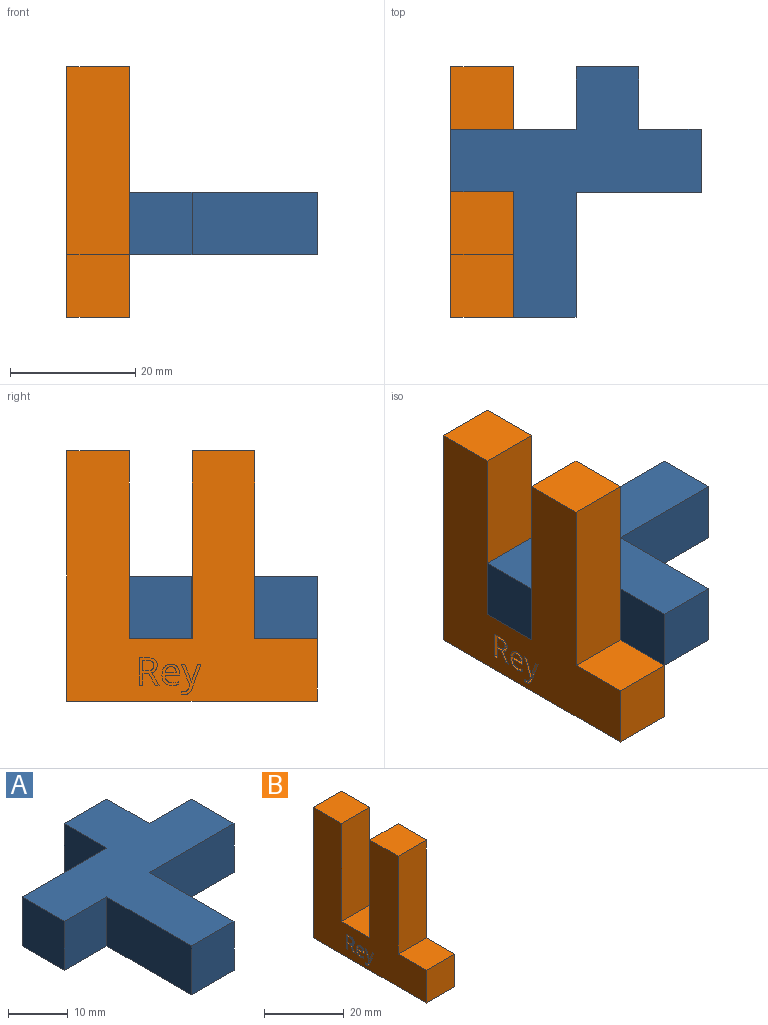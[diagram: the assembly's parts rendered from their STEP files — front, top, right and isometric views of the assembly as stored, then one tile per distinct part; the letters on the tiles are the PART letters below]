
ASSEMBLY  parts=2 mates=1
PART A: 14 faces, bbox 40x40x10 mm
  f0: plane 10x10mm, normal (1,0,0), area 100mm2, adj f3,f8,f9,f13
  f1: plane 10x10mm, normal (-1,0,0), area 100mm2, adj f3,f5,f11,f13
  f2: plane 10x10mm, normal (0,-1,0), area 100mm2, adj f3,f10,f12,f13
  f3: plane 40x40mm, normal (0,0,1), area 700mm2, adj f0,f1,f2,f4,f5,f6,f7,f8
  f4: plane 10x10mm, normal (0,1,0), area 100mm2, adj f3,f6,f7,f13
  f5: plane 20x10mm, normal (0,1,0), area 200mm2, adj f1,f3,f6,f13
  f6: plane 10x10mm, normal (-1,0,0), area 100mm2, adj f3,f4,f5,f13
  f7: plane 10x10mm, normal (1,0,0), area 100mm2, adj f3,f4,f8,f13
  f8: plane 10x10mm, normal (0,1,0), area 100mm2, adj f0,f3,f7,f13
  f9: plane 20x10mm, normal (0,-1,0), area 200mm2, adj f0,f3,f10,f13
  f10: plane 20x10mm, normal (1,0,0), area 200mm2, adj f2,f3,f9,f13
  f11: plane 10x10mm, normal (0,-1,0), area 100mm2, adj f1,f3,f12,f13
  f12: plane 20x10mm, normal (-1,0,0), area 200mm2, adj f2,f3,f11,f13
  f13: plane 40x40mm, normal (0,0,-1), area 700mm2, adj f0,f1,f2,f4,f5,f6,f7,f8
PART B: 70 faces, bbox 10x40x40 mm
  f0: plane 40x40mm, normal (-1,0,0), area 981.5mm2, adj f1,f2,f3,f4,f5,f7,f8,f9
  f1: plane 10x10mm, normal (0,0,1), area 100mm2, adj f0,f6,f7,f11
  f2: plane 10x10mm, normal (0,0,1), area 100mm2, adj f0,f4,f6,f8
  f3: plane 10x10mm, normal (0,-1,0), area 100mm2, adj f0,f5,f6,f10
  f4: plane 40x10mm, normal (0,1,0), area 400mm2, adj f0,f2,f5,f6
  f5: plane 40x10mm, normal (0,0,-1), area 400mm2, adj f0,f3,f4,f6
  f6: plane 40x40mm, normal (1,0,0), area 1000mm2, adj f1,f2,f3,f4,f5,f7,f8,f9
  f7: plane 30x10mm, normal (0,1,0), area 300mm2, adj f0,f1,f6,f9
  f8: plane 30x10mm, normal (0,-1,0), area 300mm2, adj f0,f2,f6,f9
  f9: plane 10x10mm, normal (0,0,1), area 100mm2, adj f0,f6,f7,f8
  f10: plane 10x10mm, normal (0,0,1), area 100mm2, adj f0,f3,f6,f11
  f11: plane 30x10mm, normal (0,-1,0), area 300mm2, adj f0,f1,f6,f10
  f12: extruded ~2x0.64mm, area 1.4mm2, adj f13,f30,f31,f68
  f13: extruded ~2x0.6mm, area 1.4mm2, adj f12,f14,f31,f68
  f14: extruded ~2x0.73mm, area 1.5mm2, adj f13,f15,f31,f68
  f15: plane 2x1.73mm, normal (0,0,-1), area 3.5mm2, adj f14,f30,f31,f68
  f16: extruded ~2x1.16mm, area 2.6mm2, adj f0,f17,f29,f31
  f17: extruded ~2x0.57mm, area 1.2mm2, adj f0,f16,f18,f31
  f18: extruded ~2x0.5mm, area 1.1mm2, adj f0,f17,f19,f31
  f19: plane 2x0.45mm, normal (0,1,0), area 0.9mm2, adj f0,f18,f20,f31
  f20: extruded ~2x1.06mm, area 2.2mm2, adj f0,f19,f21,f31
  f21: extruded ~2x0.79mm, area 1.7mm2, adj f0,f20,f22,f31
  f22: extruded ~2x0.89mm, area 1.9mm2, adj f0,f21,f23,f31
  f23: plane 2.28x2mm, normal (0,0,1), area 4.6mm2, adj f0,f22,f24,f31
  f24: plane 2x0.32mm, normal (0,1,0), area 0.6mm2, adj f0,f23,f25,f31
  f25: extruded ~2x1.08mm, area 2.3mm2, adj f0,f24,f26,f31
  f26: extruded ~2x0.98mm, area 2.2mm2, adj f0,f25,f27,f31
  f27: extruded ~2x1.06mm, area 2.4mm2, adj f0,f26,f28,f31
  f28: extruded ~2x1.27mm, area 2.7mm2, adj f0,f27,f29,f31
  f29: extruded ~2x1.24mm, area 2.7mm2, adj f0,f16,f28,f31
  f30: extruded ~2x0.72mm, area 1.6mm2, adj f12,f15,f31,f68
  f31: plane 3.43x2.8mm, normal (-1,0,0), area 4.4mm2, adj f12,f13,f14,f15,f16,f17,f18,f19
  f32: plane 2x0.7mm, normal (0,0,-1), area 1.4mm2, adj f33,f49,f50,f69
  f33: plane 2x1.69mm, normal (0,1,0), area 3.4mm2, adj f32,f34,f50,f69
  f34: plane 2x0.67mm, normal (0,0,1), area 1.3mm2, adj f33,f35,f50,f69
  f35: extruded ~2x0.83mm, area 1.7mm2, adj f34,f36,f50,f69
  f36: extruded ~2x0.63mm, area 1.4mm2, adj f35,f37,f50,f69
  f37: extruded ~2x0.65mm, area 1.4mm2, adj f36,f49,f50,f69
  f38: plane 2x1.84mm, normal (0,1,0), area 3.7mm2, adj f0,f39,f48,f50
  f39: plane 2x0.92mm, normal (0,0,1), area 1.8mm2, adj f0,f38,f40,f50
  f40: plane 2x1.84mm, normal (0,-0.86,0.5), area 4.2mm2, adj f0,f39,f41,f50
  f41: plane 2x0.61mm, normal (0,0,1), area 1.2mm2, adj f0,f40,f42,f50
  f42: plane 2x1.98mm, normal (0,0.86,-0.52), area 4.6mm2, adj f0,f41,f43,f50
  f43: extruded ~2x1.18mm, area 3.2mm2, adj f0,f42,f44,f50
  f44: extruded ~2x0.94mm, area 2.1mm2, adj f0,f43,f45,f50
  f45: extruded ~2x1.2mm, area 2.5mm2, adj f0,f44,f46,f50
  f46: plane 2x1.21mm, normal (0,0,-1), area 2.4mm2, adj f0,f45,f47,f50
  f47: plane 4.42x2mm, normal (0,-1,0), area 8.8mm2, adj f0,f46,f48,f50
  f48: plane 2x0.51mm, normal (0,0,1), area 1mm2, adj f0,f38,f47,f50
  f49: extruded ~2x0.8mm, area 1.7mm2, adj f32,f37,f50,f69
  f50: plane 4.42x3.11mm, normal (-1,0,0), area 5.8mm2, adj f32,f33,f34,f35,f36,f37,f38,f39
  f51: plane 2x0.54mm, normal (0,0,-1), area 1.1mm2, adj f0,f52,f66,f67
  f52: plane 3.33x2mm, normal (0,-0.93,0.37), area 7.2mm2, adj f0,f51,f53,f67
  f53: plane 2x0.47mm, normal (0,-0.93,-0.37), area 1mm2, adj f0,f52,f54,f67
  f54: extruded ~2x0.74mm, area 2mm2, adj f0,f53,f55,f67
  f55: extruded ~2x0.37mm, area 0.7mm2, adj f0,f54,f56,f67
  f56: plane 2x0.4mm, normal (0,-1,0), area 0.8mm2, adj f0,f55,f57,f67
  f57: extruded ~2x0.45mm, area 0.9mm2, adj f0,f56,f58,f67
  f58: extruded ~2x0.69mm, area 1.5mm2, adj f0,f57,f59,f67
  f59: extruded ~2x0.79mm, area 1.9mm2, adj f0,f58,f60,f67
  f60: plane 3.77x2mm, normal (0,0.94,0.35), area 8.1mm2, adj f0,f59,f61,f67
  f61: plane 2x0.54mm, normal (0,0,-1), area 1.1mm2, adj f0,f60,f62,f67
  f62: extruded ~2.29x2mm, area 4.9mm2, adj f0,f61,f63,f67
  f63: extruded ~2x0.53mm, area 1.1mm2, adj f0,f62,f64,f67
  f64: plane 2x0.02mm, normal (0,0,-1), area 0mm2, adj f0,f63,f65,f67
  f65: extruded ~2x0.93mm, area 2mm2, adj f0,f64,f66,f67
  f66: plane 2x1.89mm, normal (0,0.93,-0.36), area 4mm2, adj f0,f51,f65,f67
  f67: plane 4.8x3.11mm, normal (-1,0,0), area 4.3mm2, adj f51,f52,f53,f54,f55,f56,f57,f58
  f68: plane 1.73x0.98mm, normal (-1,0,0), area 1.4mm2, adj f12,f13,f14,f15,f30
  f69: plane 1.76x1.69mm, normal (-1,0,0), area 2.7mm2, adj f32,f33,f34,f35,f36,f37,f49
PLACE A t=(-22.76,-0.35,13.17)mm
PLACE B t=(-25.04,-0.35,30.25)mm
MATE parallel B.f9 <-> A.f13  axis (0,0,1) through (-71.78,-10.35,9.32)mm
